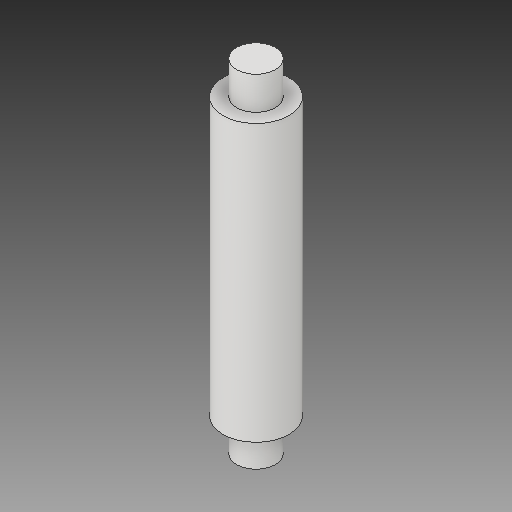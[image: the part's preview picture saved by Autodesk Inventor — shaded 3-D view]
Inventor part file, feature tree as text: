
AUTODESK INVENTOR PART (.ipt)
format: ipt  version: 2018.2 (Build 222227000, 227)  size: 95,232 bytes
history: native  units: mm
features: revolve x1, sketch x1
ambient origin geometry x8: Origin, YZ Plane, XZ Plane, XY Plane, X Axis, Y Axis, Z Axis, Center Point
bodies: Solid1 (feature_tree)
feature tree (2):
  revolve  "Revolution1"  [1 undecoded]
  sketch  "Sketch1"  dims[d0=33.5mm d1=8.0mm d2=4.7mm d3=4.0mm d4=4.0mm d5=90.0deg]
note: 1 required parameter value undecoded (feature->parameter linkage not recoverable at this tier; creation-order binding heuristic only, values carry confidence <= 0.55)
